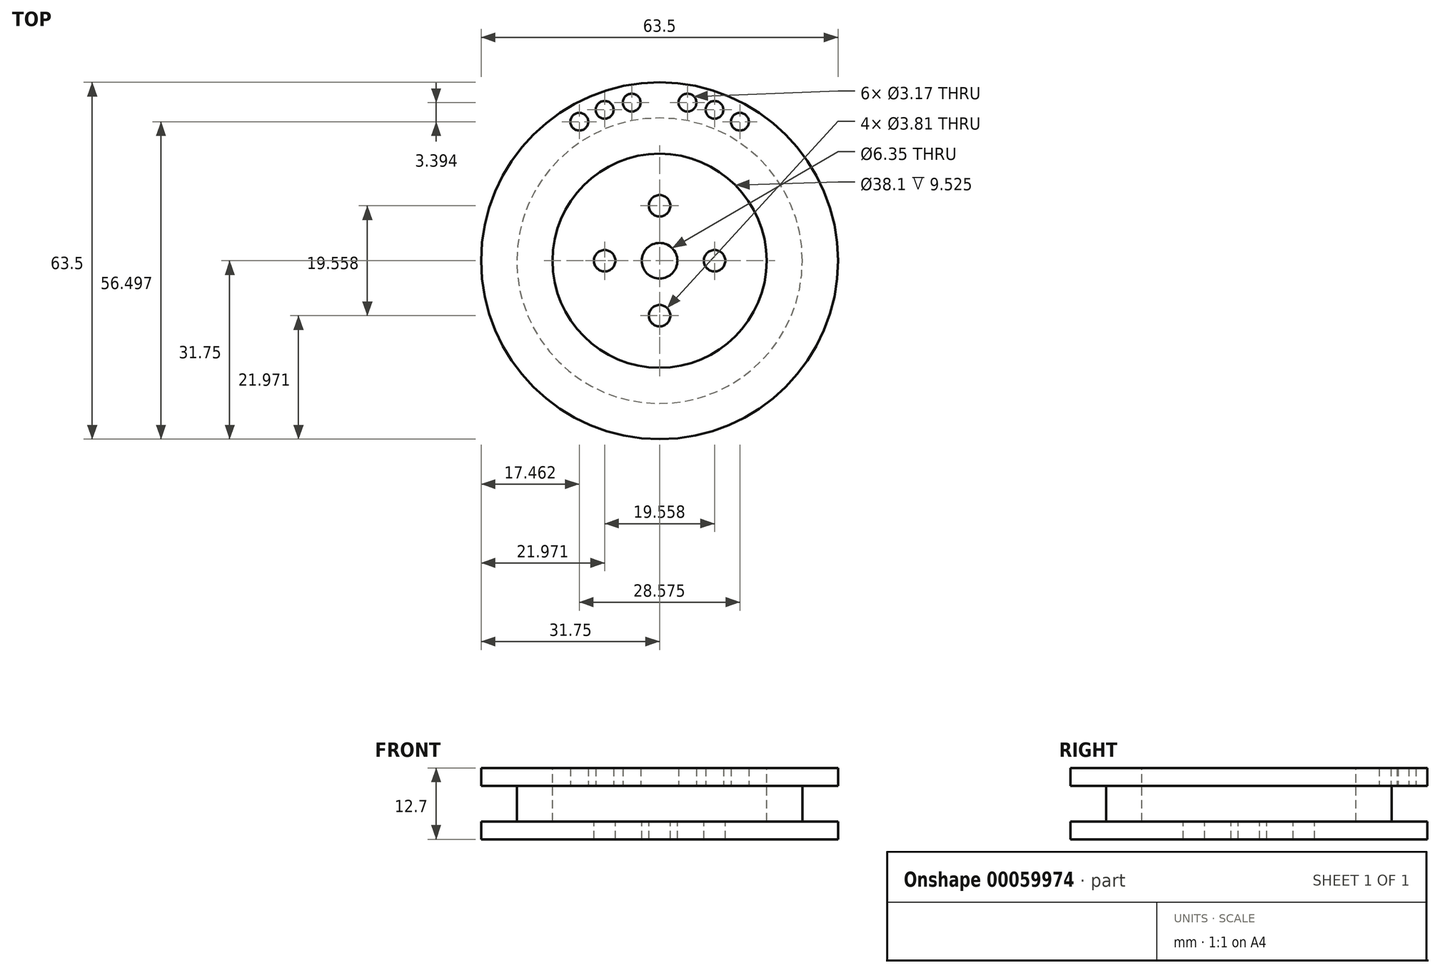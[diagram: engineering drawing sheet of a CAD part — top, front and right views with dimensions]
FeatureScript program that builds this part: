
annotation { "Feature Type Name" : "Feature", "Feature Type Description" : "" }
export const myFeature = defineFeature(function(context is Context, id is Id, definition is map)
    precondition{}
    {
        {
            var Q0;
            Q0=qCreatedBy(makeId("Top.planeOp"),FACE);
            var sketch = newSketch(context, id + "F0", { "sketchPlane" : qUnion([Q0])});
            skCircle(sketch, "E0", {"center": v(0, 0) * mm, "radius": 25.4 * mm});
            skCircle(sketch, "E1", {"center": v(0, 0) * mm, "radius": 31.75 * mm});
            skSolve(sketch);
        }
        {
            var Q0;
            Q0=makeQuery(id+"F0.imprint","IMPRINT",FACE,{"disambiguationData":[TD([[makeQuery(id+"F0.imprint","IMPRINT",EDGE,{"derivedFrom":sQuery(id+"F0.wireOp",EDGE,"E0")}),-1.0]])]});
            var Q1;
            Q1=makeQuery(id+"F0.imprint","IMPRINT",FACE,{"disambiguationData":[TD([[makeQuery(id+"F0.imprint","IMPRINT",EDGE,{"derivedFrom":sQuery(id+"F0.wireOp",EDGE,"E0")}),1.0]])]});
            extrude(context, id + "F1", {"entities" : qUnion([Q0, Q1]), "depth" : 3.17 * mm});
        }
        {
            var Q0;
            Q0=makeQuery(id+"F1.opExtrude","CAP_FACE",FACE,{"disambiguationData":[OSD([sQuery(id+"F0.wireOp",EDGE,"E1")])],"isStart":false});
            var sketch = newSketch(context, id + "F2", { "sketchPlane" : qUnion([Q0])});
            skCircle(sketch, "E2", {"center": v(0, 0) * mm, "radius": 25.4 * mm});
            skSolve(sketch);
        }
        {
            var Q0;
            Q0=makeQuery(id+"F2.imprint","IMPRINT",FACE,{"disambiguationData":[TD([[makeQuery(id+"F2.imprint","IMPRINT",EDGE,{"derivedFrom":sQuery(id+"F2.wireOp",EDGE,"E2")}),1.0]])]});
            extrude(context, id + "F3", {"entities" : qUnion([Q0]), "operationType" : NewBodyOperationType.ADD, "depth" : 6.35 * mm});
        }
        {
            var Q0;
            Q0=makeQuery(id+"F3.opExtrude","CAP_FACE",FACE,{"disambiguationData":[OSD([sQuery(id+"F2.wireOp",EDGE,"E2")])],"isStart":false});
            var sketch = newSketch(context, id + "F4", { "sketchPlane" : qUnion([Q0])});
            skCircle(sketch, "E3", {"center": v(0, 0) * mm, "radius": 31.75 * mm});
            skLineSegment(sketch, "E4", {"start": v(0, 0) * mm, "end": v(9.77, 26.85) * mm, "construction": true});
            skCircle(sketch, "E5", {"center": v(9.77, 26.85) * mm, "radius": 1.59 * mm});
            skLineSegment(sketch, "E6", {"start": v(0, 0) * mm, "end": v(0, 41.55) * mm, "construction": true});
            skCircle(sketch, "E7.MirrorC", {"center": v(-9.77, 26.85) * mm, "radius": 1.59 * mm});
            skLineSegment(sketch, "E8", {"start": v(0, 0) * mm, "end": v(14.29, 24.75) * mm, "construction": true});
            skCircle(sketch, "E9", {"center": v(14.29, 24.75) * mm, "radius": 1.59 * mm});
            skCircle(sketch, "E10.MirrorC", {"center": v(-14.29, 24.75) * mm, "radius": 1.59 * mm});
            skLineSegment(sketch, "E11", {"start": v(0, 0) * mm, "end": v(4.96, 28.14) * mm, "construction": true});
            skCircle(sketch, "E12", {"center": v(4.96, 28.14) * mm, "radius": 1.59 * mm});
            skCircle(sketch, "E13.MirrorC", {"center": v(-4.96, 28.14) * mm, "radius": 1.59 * mm});
            skSolve(sketch);
        }
        {
            var Q0;
            Q0 = qSketchRegion(id + "F4", true);
            extrude(context, id + "F5", {"entities" : qUnion([Q0]), "operationType" : NewBodyOperationType.ADD, "depth" : 3.17 * mm});
        }
        {
            var Q0;
            Q0=makeQuery(id+"F5.opExtrude","CAP_FACE",FACE,{"disambiguationData":[OSD([sQuery(id+"F4.wireOp",EDGE,"E3")])],"isStart":false});
            var sketch = newSketch(context, id + "F6", { "sketchPlane" : qUnion([Q0])});
            skCircle(sketch, "E14", {"center": v(0, 0) * mm, "radius": 9.78 * mm, "construction": true});
            skCircle(sketch, "E15", {"center": v(0, 9.78) * mm, "radius": 1.9 * mm});
            skCircle(sketch, "E16", {"center": v(0, -9.78) * mm, "radius": 1.9 * mm});
            skCircle(sketch, "E17", {"center": v(-9.78, 0) * mm, "radius": 1.9 * mm});
            skCircle(sketch, "E18", {"center": v(9.78, 0) * mm, "radius": 1.9 * mm});
            skCircle(sketch, "E19", {"center": v(0, 0) * mm, "radius": 3.18 * mm});
            skSolve(sketch);
        }
        {
            var Q0;
            Q0 = qSketchRegion(id + "F6", true);
            extrude(context, id + "F7", {"entities" : qUnion([Q0]), "operationType" : NewBodyOperationType.REMOVE, "endBound" : BoundingType.UP_TO_NEXT, "oppositeDirection" : true, "depth" : 25.4 * mm});
        }
        {
            var Q0;
            Q0=makeQuery(id+"F5.opExtrude","CAP_FACE",FACE,{"disambiguationData":[OSD([sQuery(id+"F4.wireOp",EDGE,"E3"),sQuery(id+"F4.wireOp",EDGE,"E5"),sQuery(id+"F4.wireOp",EDGE,"E7.MirrorC"),sQuery(id+"F4.wireOp",EDGE,"E9"),sQuery(id+"F4.wireOp",EDGE,"E10.MirrorC"),sQuery(id+"F4.wireOp",EDGE,"E12"),sQuery(id+"F4.wireOp",EDGE,"E13.MirrorC")])],"isStart":false});
            var sketch = newSketch(context, id + "F8", { "sketchPlane" : qUnion([Q0])});
            skCircle(sketch, "E20", {"center": v(0, 0) * mm, "radius": 19.05 * mm});
            skSolve(sketch);
        }
        {
            var Q0;
            Q0=makeQuery(id+"F8.imprint","IMPRINT",FACE,{"disambiguationData":[TD([[makeQuery(id+"F8.imprint","IMPRINT",EDGE,{"derivedFrom":sQuery(id+"F8.wireOp",EDGE,"E20")}),1.0]])]});
            extrude(context, id + "F9", {"entities" : qUnion([Q0]), "operationType" : NewBodyOperationType.REMOVE, "oppositeDirection" : true, "depth" : 9.52 * mm});
        }
    });
